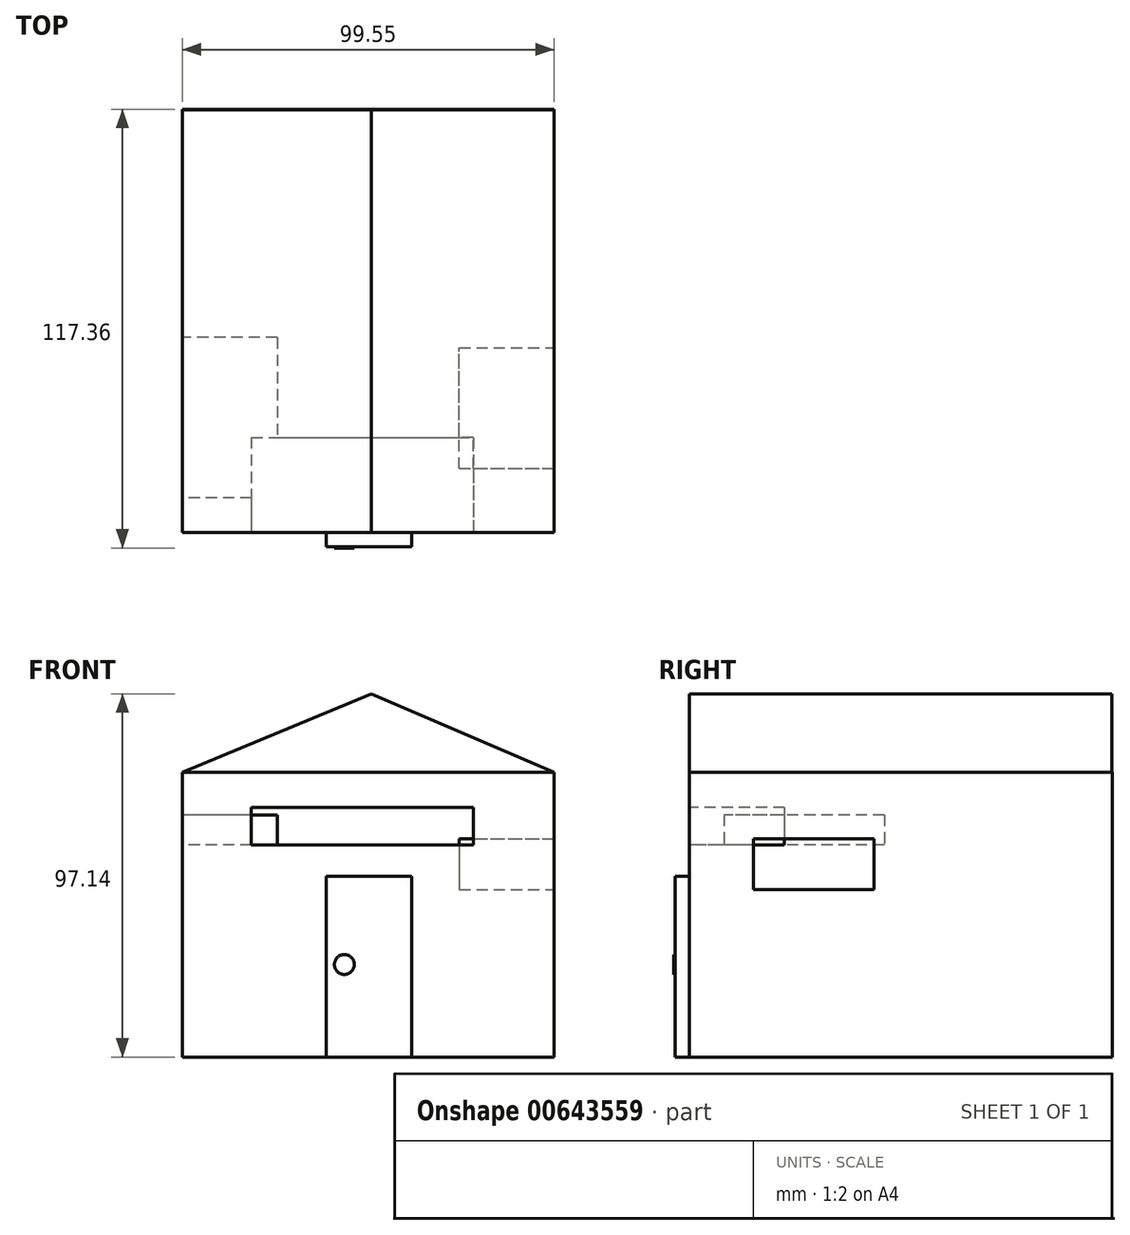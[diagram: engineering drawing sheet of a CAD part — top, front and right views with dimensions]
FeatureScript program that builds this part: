
annotation { "Feature Type Name" : "Feature", "Feature Type Description" : "" }
export const myFeature = defineFeature(function(context is Context, id is Id, definition is map)
    precondition{}
    {
        {
            var Q0;
            Q0=qCreatedBy(makeId("Top.planeOp"),FACE);
            var sketch = newSketch(context, id + "F0", { "sketchPlane" : qUnion([Q0])});
            skLineSegment(sketch, "E0.bottom", {"start": v(-50.57, 51.8) * mm, "end": v(48.98, 51.8) * mm});
            skLineSegment(sketch, "E0.top", {"start": v(-50.57, -61.37) * mm, "end": v(48.98, -61.37) * mm});
            skLineSegment(sketch, "E0.left", {"start": v(-50.57, 51.8) * mm, "end": v(-50.57, -61.37) * mm});
            skLineSegment(sketch, "E0.right", {"start": v(48.98, 51.8) * mm, "end": v(48.98, -61.37) * mm});
            skSolve(sketch);
        }
        {
            var Q0;
            Q0=makeQuery(id+"F0.imprint","IMPRINT",FACE,{"disambiguationData":[TD([[makeQuery(id+"F0.imprint","IMPRINT",EDGE,{"derivedFrom":sQuery(id+"F0.wireOp",EDGE,"E0.bottom")}),-1.0]])]});
            extrude(context, id + "F1", {"entities" : qUnion([Q0]), "depth" : 76.2 * mm, "offsetDistance" : 25.4 * mm});
        }
        {
            var Q0;
            Q0=makeQuery(id+"F1.opExtrude","SWEPT_FACE",FACE,{"disambiguationData":[OSD([sQuery(id+"F0.wireOp",EDGE,"E0.top")])]});
            var sketch = newSketch(context, id + "F2", { "sketchPlane" : qUnion([Q0])});
            skLineSegment(sketch, "E1", {"start": v(0, 97.14) * mm, "end": v(0, 76.2) * mm});
            skLineSegment(sketch, "E2", {"start": v(0, 97.14) * mm, "end": v(48.98, 76.2) * mm});
            skLineSegment(sketch, "E3", {"start": v(0, 97.14) * mm, "end": v(-50.57, 76.2) * mm});
            skSolve(sketch);
        }
        {
            var Q0;
            {var subQ0=sQuery(id+"F2.wireOp",EDGE,"E1");Q0=makeQuery(id+"F2.imprint","IMPRINT",FACE,{"disambiguationData":[TD([[makeQuery(id+"F2.imprint","IMPRINT",EDGE,{"derivedFrom":subQ0}),-1.0]])]});}
            var Q1;
            {var subQ0=sQuery(id+"F2.wireOp",EDGE,"E1");Q1=makeQuery(id+"F2.imprint","IMPRINT",FACE,{"disambiguationData":[TD([[makeQuery(id+"F2.imprint","IMPRINT",EDGE,{"derivedFrom":subQ0}),1.0]])]});}
            extrude(context, id + "F3", {"entities" : qUnion([Q0, Q1]), "oppositeDirection" : true, "depth" : 113.03 * mm, "offsetDistance" : 25.4 * mm});
        }
        {
            var Q0;
            Q0=makeQuery(id+"F1.opExtrude","SWEPT_FACE",FACE,{"disambiguationData":[OSD([sQuery(id+"F0.wireOp",EDGE,"E0.top")])]});
            var sketch = newSketch(context, id + "F4", { "sketchPlane" : qUnion([Q0])});
            skLineSegment(sketch, "E4.bottom", {"start": v(-12.02, 48.3) * mm, "end": v(10.9, 48.3) * mm});
            skLineSegment(sketch, "E4.top", {"start": v(-12.02, 0) * mm, "end": v(10.9, 0) * mm});
            skLineSegment(sketch, "E4.left", {"start": v(-12.02, 48.3) * mm, "end": v(-12.02, 0) * mm});
            skLineSegment(sketch, "E4.right", {"start": v(10.9, 48.3) * mm, "end": v(10.9, 0) * mm});
            skSolve(sketch);
        }
        {
            var Q0;
            Q0=makeQuery(id+"F1.opExtrude","SWEPT_FACE",FACE,{"disambiguationData":[OSD([sQuery(id+"F0.wireOp",EDGE,"E0.right")])]});
            var sketch = newSketch(context, id + "F5", { "sketchPlane" : qUnion([Q0])});
            skLineSegment(sketch, "E5.bottom", {"start": v(-44.3, 58.3) * mm, "end": v(-12.02, 58.3) * mm});
            skLineSegment(sketch, "E5.top", {"start": v(-44.3, 44.76) * mm, "end": v(-12.02, 44.76) * mm});
            skLineSegment(sketch, "E5.left", {"start": v(-44.3, 58.3) * mm, "end": v(-44.3, 44.76) * mm});
            skLineSegment(sketch, "E5.right", {"start": v(-12.02, 58.3) * mm, "end": v(-12.02, 44.76) * mm});
            skSolve(sketch);
        }
        {
            var Q0;
            Q0=makeQuery(id+"F5.imprint","IMPRINT",FACE,{"disambiguationData":[TD([[makeQuery(id+"F5.imprint","IMPRINT",EDGE,{"derivedFrom":sQuery(id+"F5.wireOp",EDGE,"E5.bottom")}),-1.0]])]});
            extrude(context, id + "F6", {"entities" : qUnion([Q0]), "operationType" : NewBodyOperationType.REMOVE, "oppositeDirection" : true, "depth" : 25.4 * mm, "offsetDistance" : 25.4 * mm});
        }
        {
            var Q0;
            Q0=makeQuery(id+"F4.imprint","IMPRINT",FACE,{"disambiguationData":[TD([[makeQuery(id+"F4.imprint","IMPRINT",EDGE,{"derivedFrom":sQuery(id+"F4.wireOp",EDGE,"E4.bottom")}),-1.0]])]});
            extrude(context, id + "F7", {"entities" : qUnion([Q0]), "operationType" : NewBodyOperationType.ADD, "depth" : 3.8 * mm, "offsetDistance" : 25.4 * mm});
        }
        {
            var Q0;
            Q0=makeQuery(id+"F1.opExtrude","SWEPT_FACE",FACE,{"disambiguationData":[OSD([sQuery(id+"F0.wireOp",EDGE,"E0.top")])]});
            var sketch = newSketch(context, id + "F8", { "sketchPlane" : qUnion([Q0])});
            skLineSegment(sketch, "E6.bottom", {"start": v(-32.03, 66.7) * mm, "end": v(27.35, 66.7) * mm});
            skLineSegment(sketch, "E6.top", {"start": v(-32.03, 56.7) * mm, "end": v(27.35, 56.7) * mm});
            skLineSegment(sketch, "E6.left", {"start": v(-32.03, 66.7) * mm, "end": v(-32.03, 56.7) * mm});
            skLineSegment(sketch, "E6.right", {"start": v(27.35, 66.7) * mm, "end": v(27.35, 56.7) * mm});
            skSolve(sketch);
        }
        {
            var Q0;
            Q0=makeQuery(id+"F8.imprint","IMPRINT",FACE,{"disambiguationData":[TD([[makeQuery(id+"F8.imprint","IMPRINT",EDGE,{"derivedFrom":sQuery(id+"F8.wireOp",EDGE,"E6.bottom")}),-1.0]])]});
            extrude(context, id + "F9", {"entities" : qUnion([Q0]), "operationType" : NewBodyOperationType.REMOVE, "oppositeDirection" : true, "depth" : 25.4 * mm, "offsetDistance" : 25.4 * mm});
        }
        {
            var Q0;
            Q0=makeQuery(id+"F1.opExtrude","SWEPT_FACE",FACE,{"disambiguationData":[OSD([sQuery(id+"F0.wireOp",EDGE,"E0.left")])]});
            var sketch = newSketch(context, id + "F10", { "sketchPlane" : qUnion([Q0])});
            skLineSegment(sketch, "E7.bottom", {"start": v(9.28, 64.76) * mm, "end": v(52.2, 64.76) * mm});
            skLineSegment(sketch, "E7.top", {"start": v(9.28, 56.7) * mm, "end": v(52.2, 56.7) * mm});
            skLineSegment(sketch, "E7.left", {"start": v(9.28, 64.76) * mm, "end": v(9.28, 56.7) * mm});
            skLineSegment(sketch, "E7.right", {"start": v(52.2, 64.76) * mm, "end": v(52.2, 56.7) * mm});
            skSolve(sketch);
        }
        {
            var Q0;
            Q0=makeQuery(id+"F10.imprint","IMPRINT",FACE,{"disambiguationData":[TD([[makeQuery(id+"F10.imprint","IMPRINT",EDGE,{"derivedFrom":sQuery(id+"F10.wireOp",EDGE,"E7.bottom")}),-1.0]])]});
            extrude(context, id + "F11", {"entities" : qUnion([Q0]), "operationType" : NewBodyOperationType.REMOVE, "oppositeDirection" : true, "depth" : 25.4 * mm, "offsetDistance" : 25.4 * mm});
        }
        {
            var Q0;
            Q0=makeQuery(id+"F7.opExtrude","CAP_FACE",FACE,{"disambiguationData":[OSD([sQuery(id+"F4.wireOp",EDGE,"E4.bottom"),sQuery(id+"F4.wireOp",EDGE,"E4.top"),sQuery(id+"F4.wireOp",EDGE,"E4.left"),sQuery(id+"F4.wireOp",EDGE,"E4.right")])],"isStart":false});
            var sketch = newSketch(context, id + "F12", { "sketchPlane" : qUnion([Q0])});
            skCircle(sketch, "E8", {"center": v(-7.18, 24.75) * mm, "radius": 2.66 * mm});
            skSolve(sketch);
        }
        {
            var Q0;
            Q0=makeQuery(id+"F12.imprint","IMPRINT",FACE,{"disambiguationData":[TD([[makeQuery(id+"F12.imprint","IMPRINT",EDGE,{"derivedFrom":sQuery(id+"F12.wireOp",EDGE,"E8")}),1.0]])]});
            extrude(context, id + "F13", {"entities" : qUnion([Q0]), "operationType" : NewBodyOperationType.ADD, "depth" : 0.38 * mm, "offsetDistance" : 25.4 * mm});
        }
    });
